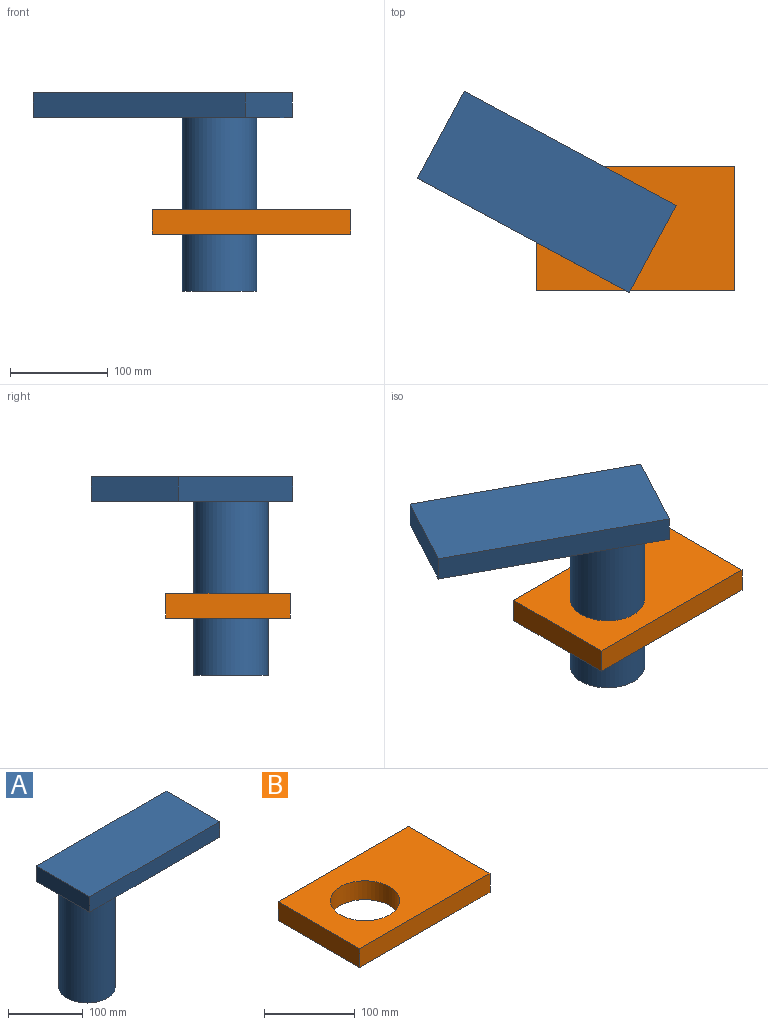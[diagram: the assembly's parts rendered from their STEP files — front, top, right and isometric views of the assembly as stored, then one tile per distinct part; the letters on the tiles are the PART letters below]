
ASSEMBLY  parts=2 mates=1
PART A: 8 faces, bbox 246.5x101.1x203.2 mm
  f0: cylinder r=38.1mm len=177.8mm, axis (0,0,-1), area 42563.4mm2, adj f1,f7
  f1: plane 76.2x76.2mm, normal (0,0,-1), area 4560.4mm2, adj f0
  f2: plane 246.51x25.4mm, normal (0,1,0), area 6261.4mm2, adj f3,f5,f6,f7
  f3: plane 101.13x25.4mm, normal (-1,0,0), area 2568.7mm2, adj f2,f4,f6,f7
  f4: plane 246.51x25.4mm, normal (0,-1,0), area 6261.4mm2, adj f3,f5,f6,f7
  f5: plane 101.13x25.4mm, normal (1,0,0), area 2568.7mm2, adj f2,f4,f6,f7
  f6: plane 246.51x101.13mm, normal (0,0,1), area 24930.2mm2, adj f2,f3,f4,f5
  f7: plane 246.51x101.13mm, normal (0,0,-1), area 20369.9mm2, adj f0,f2,f3,f4,f5
PART B: 7 faces, bbox 203.2x127x25.4 mm
  f0: plane 203.2x25.4mm, normal (0,1,0), area 5161.3mm2, adj f1,f4,f5,f6
  f1: plane 127x25.4mm, normal (-1,0,0), area 3225.8mm2, adj f0,f2,f5,f6
  f2: plane 203.2x25.4mm, normal (0,-1,0), area 5161.3mm2, adj f1,f4,f5,f6
  f3: cylinder r=38.1mm len=76.2mm, axis (0,0,-1), area 6080.5mm2, adj f5,f6
  f4: plane 127x25.4mm, normal (1,0,0), area 3225.8mm2, adj f0,f2,f5,f6
  f5: plane 203.2x127mm, normal (0,0,1), area 21246mm2, adj f0,f1,f2,f3,f4
  f6: plane 203.2x127mm, normal (0,0,-1), area 21246mm2, adj f0,f1,f2,f3,f4
PLACE A rot(axis=(0,0,1),151.7deg) t=(-8.2,-367.48,181.76)mm
PLACE B t=(-21.39,-327.87,240.28)mm fixed
MATE cylindrical A.f0 <-> B.f3  axis (0,0,-1) through (10.72,-377.68,181.76)mm
